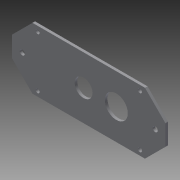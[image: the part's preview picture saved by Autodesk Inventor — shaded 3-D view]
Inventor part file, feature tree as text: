
AUTODESK INVENTOR PART (.ipt)
format: ipt  version: 2015 SP1 (Build 190203100, 203)  size: 167,424 bytes
history: native  units: in
note: dims shown in document units (in); Inventor stores cm internally (conversion verified against a paired STEP export)
features: extrude x4, sketch x4, projected_geometry x3
ambient origin geometry x8: Origin, YZ Plane, XZ Plane, XY Plane, X Axis, Y Axis, Z Axis, Center Point
bodies: Solid1 (feature_tree)
feature tree (11):
  extrude  "Extrusion1"  Depth=3.0in
  extrude  "Extrusion2"  Depth=0.125in
  extrude  "Extrusion3"  Depth=2.75in
  extrude  "Extrusion4"  Depth=0.125in
  sketch  "Sketch1"  dims[d0=5.5in d1=3.0in]
  sketch  "Sketch2"  dims[d2=0.125in d3=0.0in d4=0.25in]
  projected_geometry  "Projected Loop1"
  sketch  "Sketch3"  dims[d5=0.25in d6=2.75in]
  projected_geometry  "Projected Loop2"
  sketch  "Sketch4"  dims[d7=0.25in d8=5.25in d9=0.25in d10=5.25in d11=2.75in d12=2.5in d13=1.5in d14=1.5in d15=4.1in d16=0.2in d17=0.2in d18=0.2in d19=0.2in d20=0.875in d21=1.125in d22=0.125in d23=0.0in d24=1.0in d25=1.0in d26=1.0in d27=1.0in d28=1.0in d29=1.0in d30=0.125in d31=0.0in d32=0.25in d33=0.5in d34=1.5in d35=0.25in d36=6.0in d37=1.5in d38=0.125in d39=0.0in]
  projected_geometry  "Projected Loop3"
